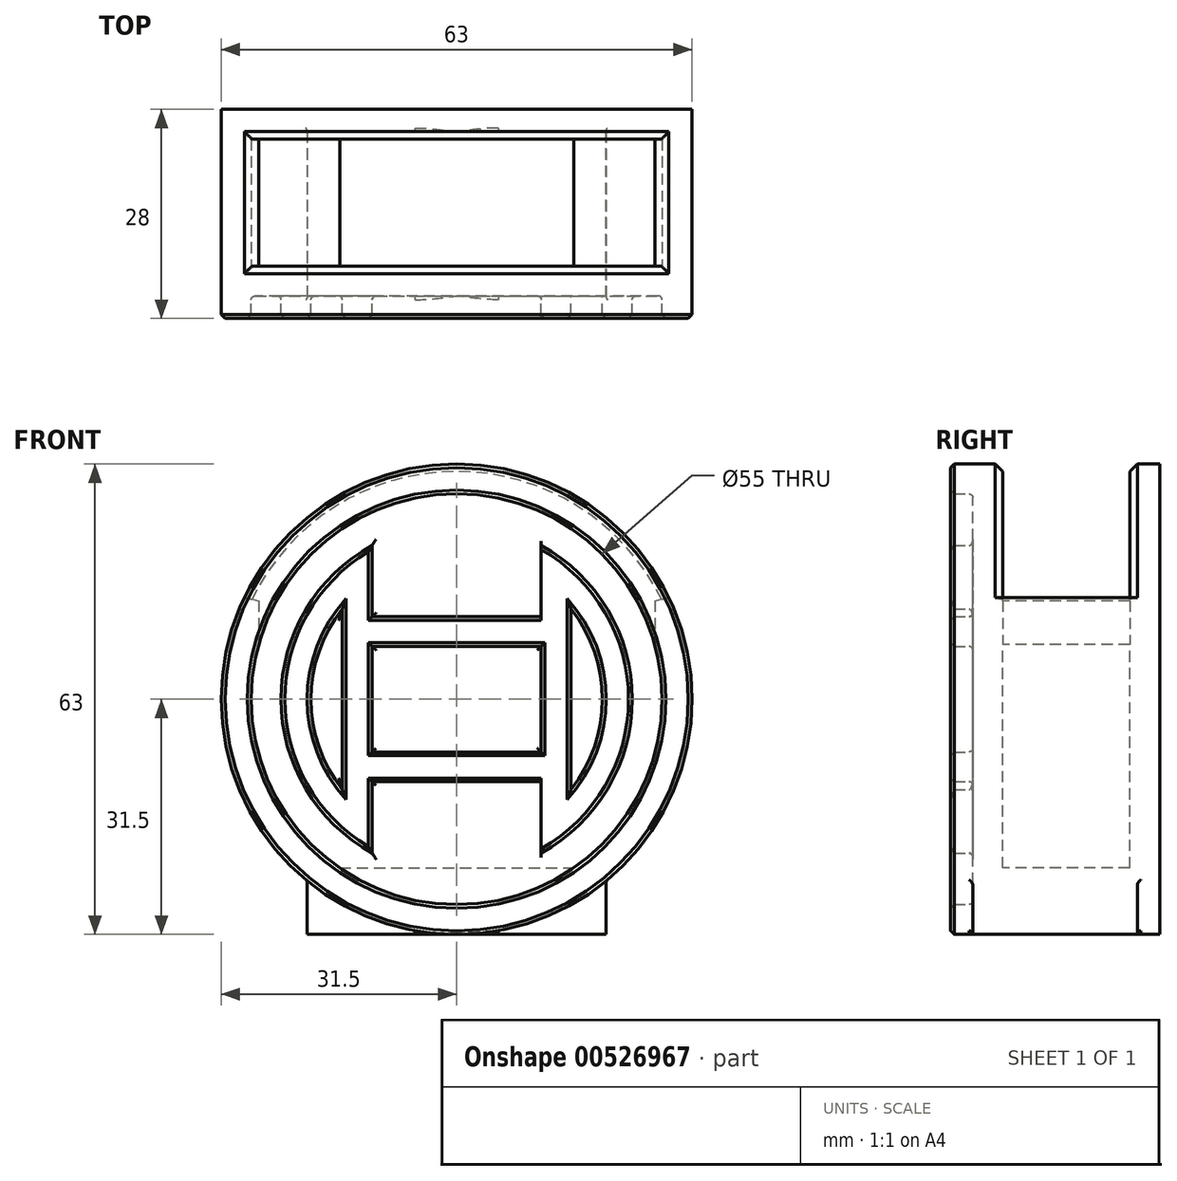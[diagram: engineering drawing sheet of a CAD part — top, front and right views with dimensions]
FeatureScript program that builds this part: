
annotation { "Feature Type Name" : "Feature", "Feature Type Description" : "" }
export const myFeature = defineFeature(function(context is Context, id is Id, definition is map)
    precondition{}
    {
        {
            var Q0;
            Q0=qCreatedBy(makeId("Front.planeOp"),FACE);
            var sketch = newSketch(context, id + "F0", { "sketchPlane" : qUnion([Q0])});
            skCircle(sketch, "E0", {"center": v(0, 0) * mm, "radius": 31.5 * mm});
            skCircle(sketch, "E1", {"center": v(0, 0) * mm, "radius": 27.5 * mm});
            skLineSegment(sketch, "E2", {"start": v(-15.3, 12.1) * mm, "end": v(-15.3, -12.1) * mm});
            skLineSegment(sketch, "E3", {"start": v(15.3, 12.1) * mm, "end": v(15.3, -12.1) * mm});
            skArc(sketch, "E4", {"start": v(-15.3, 12.1) * mm, "mid": v(-19.5, 0) * mm, "end": v(-15.3, -12.1) * mm});
            skArc(sketch, "E5", {"start": v(15.3, 12.1) * mm, "mid": v(19.5, 0) * mm, "end": v(15.3, -12.1) * mm});
            skLineSegment(sketch, "E6", {"start": v(-11.3, 20.6) * mm, "end": v(-11.3, -20.6) * mm});
            skLineSegment(sketch, "E7", {"start": v(11.3, 20.6) * mm, "end": v(11.3, -20.6) * mm});
            skArc(sketch, "E8", {"start": v(-11.3, 20.6) * mm, "mid": v(-23.5, 0) * mm, "end": v(-11.3, -20.6) * mm});
            skArc(sketch, "E9", {"start": v(11.3, 20.6) * mm, "mid": v(23.5, 0) * mm, "end": v(11.3, -20.6) * mm});
            skLineSegment(sketch, "E10", {"start": v(-11.3, 11.06) * mm, "end": v(11.3, 11.06) * mm});
            skLineSegment(sketch, "E11", {"start": v(-11.3, -11.06) * mm, "end": v(11.3, -11.06) * mm});
            skLineSegment(sketch, "E12", {"start": v(-11.3, 7.06) * mm, "end": v(11.3, 7.06) * mm});
            skLineSegment(sketch, "E13", {"start": v(-11.3, -7.06) * mm, "end": v(11.3, -7.06) * mm});
            skLineSegment(sketch, "E14", {"start": v(0, -11.06) * mm, "end": v(0, -27.5) * mm, "construction": true});
            skLineSegment(sketch, "E15", {"start": v(0, 11.06) * mm, "end": v(0, 27.5) * mm, "construction": true});
            skSolve(sketch);
        }
        {
            var Q0;
            Q0=makeQuery(id+"F0.imprint","IMPRINT",FACE,{"disambiguationData":[TD([[makeQuery(id+"F0.imprint","IMPRINT",EDGE,{"derivedFrom":sQuery(id+"F0.wireOp",EDGE,"E2")}),1.0]])]});
            var Q1;
            Q1=makeQuery(id+"F0.imprint","IMPRINT",FACE,{"disambiguationData":[TD([[makeQuery(id+"F0.imprint","IMPRINT",EDGE,{"derivedFrom":sQuery(id+"F0.wireOp",EDGE,"E3")}),-1.0]])]});
            var Q2;
            {var subQ0=sQuery(id+"F0.wireOp",EDGE,"E10");Q2=makeQuery(id+"F0.imprint","IMPRINT",FACE,{"disambiguationData":[TD([[makeQuery(id+"F0.imprint","IMPRINT",EDGE,{"derivedFrom":subQ0}),-1.0]])]});}
            var Q3;
            {var subQ0=sQuery(id+"F0.wireOp",EDGE,"E11");Q3=makeQuery(id+"F0.imprint","IMPRINT",FACE,{"disambiguationData":[TD([[makeQuery(id+"F0.imprint","IMPRINT",EDGE,{"derivedFrom":subQ0}),1.0]])]});}
            var Q4;
            Q4=makeQuery(id+"F0.imprint","IMPRINT",FACE,{"disambiguationData":[TD([[makeQuery(id+"F0.imprint","IMPRINT",EDGE,{"derivedFrom":sQuery(id+"F0.wireOp",EDGE,"E0")}),1.0]])]});
            var Q5;
            Q5=makeQuery(id+"F0.imprint","IMPRINT",FACE,{"disambiguationData":[TD([[makeQuery(id+"F0.imprint","IMPRINT",EDGE,{"derivedFrom":sQuery(id+"F0.wireOp",EDGE,"E1")}),1.0]])]});
            var Q6;
            Q6=makeQuery(id+"F0.imprint","IMPRINT",FACE,{"disambiguationData":[TD([[makeQuery(id+"F0.imprint","IMPRINT",EDGE,{"derivedFrom":sQuery(id+"F0.wireOp",EDGE,"E2")}),-1.0]])]});
            var Q7;
            {var subQ0=sQuery(id+"F0.wireOp",EDGE,"E12");Q7=makeQuery(id+"F0.imprint","IMPRINT",FACE,{"disambiguationData":[TD([[makeQuery(id+"F0.imprint","IMPRINT",EDGE,{"derivedFrom":subQ0}),-1.0]])]});}
            var Q8;
            Q8=makeQuery(id+"F0.imprint","IMPRINT",FACE,{"disambiguationData":[TD([[makeQuery(id+"F0.imprint","IMPRINT",EDGE,{"derivedFrom":sQuery(id+"F0.wireOp",EDGE,"E3")}),1.0]])]});
            extrude(context, id + "F1", {"entities" : qUnion([Q0, Q1, Q2, Q3, Q4, Q5, Q6, Q7, Q8]), "oppositeDirection" : true, "depth" : 25 * mm, "offsetDistance" : 25 * mm});
        }
        {
            var Q0;
            Q0=makeQuery(id+"F1.opExtrude","CAP_FACE",FACE,{"disambiguationData":[OSD([sQuery(id+"F0.wireOp",EDGE,"E0")])],"isStart":true});
            var Q1;
            Q1=makeQuery(id+"F1.opExtrude","SWEPT_BODY",BODY,{"disambiguationData":[OSD([sQuery(id+"F0.wireOp",EDGE,"E0")])]});
            shell(context, id + "F2", {"isHollow" : true, "entities" : qUnion([Q0]), "parts" : qUnion([Q1]), "thickness" : 4 * mm});
        }
        {
            var Q0;
            Q0=makeQuery(id+"F0.imprint","IMPRINT",FACE,{"disambiguationData":[TD([[makeQuery(id+"F0.imprint","IMPRINT",EDGE,{"derivedFrom":sQuery(id+"F0.wireOp",EDGE,"E0")}),1.0]])]});
            var Q1;
            Q1=makeQuery(id+"F0.imprint","IMPRINT",FACE,{"disambiguationData":[TD([[makeQuery(id+"F0.imprint","IMPRINT",EDGE,{"derivedFrom":sQuery(id+"F0.wireOp",EDGE,"E2")}),1.0]])]});
            var Q2;
            {var subQ0=sQuery(id+"F0.wireOp",EDGE,"E10");Q2=makeQuery(id+"F0.imprint","IMPRINT",FACE,{"disambiguationData":[TD([[makeQuery(id+"F0.imprint","IMPRINT",EDGE,{"derivedFrom":subQ0}),-1.0]])]});}
            var Q3;
            {var subQ0=sQuery(id+"F0.wireOp",EDGE,"E11");Q3=makeQuery(id+"F0.imprint","IMPRINT",FACE,{"disambiguationData":[TD([[makeQuery(id+"F0.imprint","IMPRINT",EDGE,{"derivedFrom":subQ0}),1.0]])]});}
            var Q4;
            Q4=makeQuery(id+"F0.imprint","IMPRINT",FACE,{"disambiguationData":[TD([[makeQuery(id+"F0.imprint","IMPRINT",EDGE,{"derivedFrom":sQuery(id+"F0.wireOp",EDGE,"E3")}),-1.0]])]});
            extrude(context, id + "F3", {"entities" : qUnion([Q0, Q1, Q2, Q3, Q4]), "operationType" : NewBodyOperationType.ADD, "depth" : 3 * mm, "offsetDistance" : 25 * mm});
        }
        {
            var Q0;
            Q0=makeQuery(id+"F3.opExtrude","CAP_EDGE",EDGE,{"disambiguationData":[OSD([sQuery(id+"F0.wireOp",EDGE,"E1")])],"isStart":true});
            var Q1;
            {var subQ0=sQuery(id+"F0.wireOp",EDGE,"E6");Q1=makeQuery(id+"F3.opExtrude","CAP_EDGE",EDGE,{"disambiguationData":[OSD([subQ0]),TDD([makeQuery(id+"F0.imprint","IMPRINT",EDGE,{"disambiguationData":[TD([[makeQuery(id+"F0.imprint","INTERSECT",VERTEX,{"disambiguationData":[OD(0.0)],"derivedFrom":[subQ0,sQuery(id+"F0.wireOp",EDGE,"E8")]}),-1.0]])],"derivedFrom":subQ0})])],"isStart":true});}
            var Q2;
            Q2=makeQuery(id+"F3.opExtrude","CAP_EDGE",EDGE,{"disambiguationData":[OSD([sQuery(id+"F0.wireOp",EDGE,"E10")])],"isStart":true});
            var Q3;
            {var subQ0=sQuery(id+"F0.wireOp",EDGE,"E7");Q3=makeQuery(id+"F3.opExtrude","CAP_EDGE",EDGE,{"disambiguationData":[OSD([subQ0]),TDD([makeQuery(id+"F0.imprint","IMPRINT",EDGE,{"disambiguationData":[TD([[makeQuery(id+"F0.imprint","INTERSECT",VERTEX,{"disambiguationData":[OD(0.0)],"derivedFrom":[subQ0,sQuery(id+"F0.wireOp",EDGE,"E9")]}),-1.0]])],"derivedFrom":subQ0})])],"isStart":true});}
            var Q4;
            Q4=makeQuery(id+"F3.opExtrude","CAP_EDGE",EDGE,{"disambiguationData":[OSD([sQuery(id+"F0.wireOp",EDGE,"E8")])],"isStart":true});
            var Q5;
            Q5=makeQuery(id+"F3.opExtrude","CAP_EDGE",EDGE,{"disambiguationData":[OSD([sQuery(id+"F0.wireOp",EDGE,"E9")])],"isStart":true});
            var Q6;
            {var subQ0=sQuery(id+"F0.wireOp",EDGE,"E6");Q6=makeQuery(id+"F3.opExtrude","CAP_EDGE",EDGE,{"disambiguationData":[OSD([subQ0]),TDD([makeQuery(id+"F0.imprint","IMPRINT",EDGE,{"disambiguationData":[TD([[makeQuery(id+"F0.imprint","INTERSECT",VERTEX,{"disambiguationData":[OD(1.0)],"derivedFrom":[subQ0,sQuery(id+"F0.wireOp",EDGE,"E8")]}),1.0]])],"derivedFrom":subQ0})])],"isStart":true});}
            var Q7;
            Q7=makeQuery(id+"F3.opExtrude","CAP_EDGE",EDGE,{"disambiguationData":[OSD([sQuery(id+"F0.wireOp",EDGE,"E11")])],"isStart":true});
            var Q8;
            {var subQ0=sQuery(id+"F0.wireOp",EDGE,"E7");Q8=makeQuery(id+"F3.opExtrude","CAP_EDGE",EDGE,{"disambiguationData":[OSD([subQ0]),TDD([makeQuery(id+"F0.imprint","IMPRINT",EDGE,{"disambiguationData":[TD([[makeQuery(id+"F0.imprint","INTERSECT",VERTEX,{"disambiguationData":[OD(1.0)],"derivedFrom":[subQ0,sQuery(id+"F0.wireOp",EDGE,"E9")]}),1.0]])],"derivedFrom":subQ0})])],"isStart":true});}
            var Q9;
            Q9=makeQuery(id+"F3.opExtrude","CAP_EDGE",EDGE,{"disambiguationData":[OSD([sQuery(id+"F0.wireOp",EDGE,"E12")])],"isStart":true});
            var Q10;
            {var subQ0=sQuery(id+"F0.wireOp",EDGE,"E6");Q10=makeQuery(id+"F3.opExtrude","CAP_EDGE",EDGE,{"disambiguationData":[OSD([subQ0]),TDD([makeQuery(id+"F0.imprint","IMPRINT",EDGE,{"disambiguationData":[TD([[makeQuery(id+"F0.imprint","INTERSECT",VERTEX,{"derivedFrom":[subQ0,sQuery(id+"F0.wireOp",EDGE,"E12")]}),-1.0]])],"derivedFrom":subQ0})])],"isStart":true});}
            var Q11;
            Q11=makeQuery(id+"F3.opExtrude","CAP_EDGE",EDGE,{"disambiguationData":[OSD([sQuery(id+"F0.wireOp",EDGE,"E13")])],"isStart":true});
            var Q12;
            {var subQ0=sQuery(id+"F0.wireOp",EDGE,"E7");Q12=makeQuery(id+"F3.opExtrude","CAP_EDGE",EDGE,{"disambiguationData":[OSD([subQ0]),TDD([makeQuery(id+"F0.imprint","IMPRINT",EDGE,{"disambiguationData":[TD([[makeQuery(id+"F0.imprint","INTERSECT",VERTEX,{"derivedFrom":[subQ0,sQuery(id+"F0.wireOp",EDGE,"E12")]}),-1.0]])],"derivedFrom":subQ0})])],"isStart":true});}
            var Q13;
            Q13=makeQuery(id+"F3.opExtrude","CAP_EDGE",EDGE,{"disambiguationData":[OSD([sQuery(id+"F0.wireOp",EDGE,"E5")])],"isStart":true});
            var Q14;
            Q14=makeQuery(id+"F3.opExtrude","CAP_EDGE",EDGE,{"disambiguationData":[OSD([sQuery(id+"F0.wireOp",EDGE,"E3")])],"isStart":true});
            var Q15;
            Q15=makeQuery(id+"F3.opExtrude","CAP_EDGE",EDGE,{"disambiguationData":[OSD([sQuery(id+"F0.wireOp",EDGE,"E4")])],"isStart":true});
            var Q16;
            Q16=makeQuery(id+"F3.opExtrude","CAP_EDGE",EDGE,{"disambiguationData":[OSD([sQuery(id+"F0.wireOp",EDGE,"E2")])],"isStart":true});
            fillet(context, id + "F4", {"entities" : qUnion([Q0, Q1, Q2, Q3, Q4, Q5, Q6, Q7, Q8, Q9, Q10, Q11, Q12, Q13, Q14, Q15, Q16]), "radius" : .5 * mm, "tangentPropagation" : true, "allowEdgeOverflow" : false});
        }
        {
            var Q0;
            Q0=makeQuery(id+"F3.opExtrude","CAP_EDGE",EDGE,{"disambiguationData":[OSD([sQuery(id+"F0.wireOp",EDGE,"E0")])],"isStart":false});
            var Q1;
            Q1=makeQuery(id+"F3.opExtrude","CAP_EDGE",EDGE,{"disambiguationData":[OSD([sQuery(id+"F0.wireOp",EDGE,"E8")])],"isStart":false});
            var Q2;
            {var subQ0=sQuery(id+"F0.wireOp",EDGE,"E6");Q2=makeQuery(id+"F3.opExtrude","CAP_EDGE",EDGE,{"disambiguationData":[OSD([subQ0]),TDD([makeQuery(id+"F0.imprint","IMPRINT",EDGE,{"disambiguationData":[TD([[makeQuery(id+"F0.imprint","INTERSECT",VERTEX,{"disambiguationData":[OD(1.0)],"derivedFrom":[subQ0,sQuery(id+"F0.wireOp",EDGE,"E8")]}),1.0]])],"derivedFrom":subQ0})])],"isStart":false});}
            var Q3;
            Q3=makeQuery(id+"F3.opExtrude","CAP_EDGE",EDGE,{"disambiguationData":[OSD([sQuery(id+"F0.wireOp",EDGE,"E11")])],"isStart":false});
            var Q4;
            {var subQ0=sQuery(id+"F0.wireOp",EDGE,"E7");Q4=makeQuery(id+"F3.opExtrude","CAP_EDGE",EDGE,{"disambiguationData":[OSD([subQ0]),TDD([makeQuery(id+"F0.imprint","IMPRINT",EDGE,{"disambiguationData":[TD([[makeQuery(id+"F0.imprint","INTERSECT",VERTEX,{"disambiguationData":[OD(1.0)],"derivedFrom":[subQ0,sQuery(id+"F0.wireOp",EDGE,"E9")]}),1.0]])],"derivedFrom":subQ0})])],"isStart":false});}
            var Q5;
            Q5=makeQuery(id+"F3.opExtrude","CAP_EDGE",EDGE,{"disambiguationData":[OSD([sQuery(id+"F0.wireOp",EDGE,"E9")])],"isStart":false});
            var Q6;
            Q6=makeQuery(id+"F3.opExtrude","CAP_EDGE",EDGE,{"disambiguationData":[OSD([sQuery(id+"F0.wireOp",EDGE,"E13")])],"isStart":false});
            var Q7;
            {var subQ0=sQuery(id+"F0.wireOp",EDGE,"E6");Q7=makeQuery(id+"F3.opExtrude","CAP_EDGE",EDGE,{"disambiguationData":[OSD([subQ0]),TDD([makeQuery(id+"F0.imprint","IMPRINT",EDGE,{"disambiguationData":[TD([[makeQuery(id+"F0.imprint","INTERSECT",VERTEX,{"derivedFrom":[subQ0,sQuery(id+"F0.wireOp",EDGE,"E12")]}),-1.0]])],"derivedFrom":subQ0})])],"isStart":false});}
            var Q8;
            {var subQ0=sQuery(id+"F0.wireOp",EDGE,"E7");Q8=makeQuery(id+"F3.opExtrude","CAP_EDGE",EDGE,{"disambiguationData":[OSD([subQ0]),TDD([makeQuery(id+"F0.imprint","IMPRINT",EDGE,{"disambiguationData":[TD([[makeQuery(id+"F0.imprint","INTERSECT",VERTEX,{"derivedFrom":[subQ0,sQuery(id+"F0.wireOp",EDGE,"E12")]}),-1.0]])],"derivedFrom":subQ0})])],"isStart":false});}
            var Q9;
            Q9=makeQuery(id+"F3.opExtrude","CAP_EDGE",EDGE,{"disambiguationData":[OSD([sQuery(id+"F0.wireOp",EDGE,"E4")])],"isStart":false});
            var Q10;
            Q10=makeQuery(id+"F3.opExtrude","CAP_EDGE",EDGE,{"disambiguationData":[OSD([sQuery(id+"F0.wireOp",EDGE,"E2")])],"isStart":false});
            var Q11;
            Q11=makeQuery(id+"F3.opExtrude","CAP_EDGE",EDGE,{"disambiguationData":[OSD([sQuery(id+"F0.wireOp",EDGE,"E12")])],"isStart":false});
            var Q12;
            Q12=makeQuery(id+"F3.opExtrude","CAP_EDGE",EDGE,{"disambiguationData":[OSD([sQuery(id+"F0.wireOp",EDGE,"E10")])],"isStart":false});
            var Q13;
            {var subQ0=sQuery(id+"F0.wireOp",EDGE,"E6");Q13=makeQuery(id+"F3.opExtrude","CAP_EDGE",EDGE,{"disambiguationData":[OSD([subQ0]),TDD([makeQuery(id+"F0.imprint","IMPRINT",EDGE,{"disambiguationData":[TD([[makeQuery(id+"F0.imprint","INTERSECT",VERTEX,{"disambiguationData":[OD(0.0)],"derivedFrom":[subQ0,sQuery(id+"F0.wireOp",EDGE,"E8")]}),-1.0]])],"derivedFrom":subQ0})])],"isStart":false});}
            var Q14;
            {var subQ0=sQuery(id+"F0.wireOp",EDGE,"E7");Q14=makeQuery(id+"F3.opExtrude","CAP_EDGE",EDGE,{"disambiguationData":[OSD([subQ0]),TDD([makeQuery(id+"F0.imprint","IMPRINT",EDGE,{"disambiguationData":[TD([[makeQuery(id+"F0.imprint","INTERSECT",VERTEX,{"disambiguationData":[OD(0.0)],"derivedFrom":[subQ0,sQuery(id+"F0.wireOp",EDGE,"E9")]}),-1.0]])],"derivedFrom":subQ0})])],"isStart":false});}
            var Q15;
            Q15=makeQuery(id+"F3.opExtrude","CAP_EDGE",EDGE,{"disambiguationData":[OSD([sQuery(id+"F0.wireOp",EDGE,"E3")])],"isStart":false});
            var Q16;
            Q16=makeQuery(id+"F3.opExtrude","CAP_EDGE",EDGE,{"disambiguationData":[OSD([sQuery(id+"F0.wireOp",EDGE,"E5")])],"isStart":false});
            var Q17;
            Q17=makeQuery(id+"F3.opExtrude","CAP_EDGE",EDGE,{"disambiguationData":[OSD([sQuery(id+"F0.wireOp",EDGE,"E1")])],"isStart":false});
            chamfer(context, id + "F5", {"entities" : qUnion([Q0, Q1, Q2, Q3, Q4, Q5, Q6, Q7, Q8, Q9, Q10, Q11, Q12, Q13, Q14, Q15, Q16, Q17]), "width" : .5 * mm, "tangentPropagation" : true});
        }
        {
            var Q0;
            Q0=qCreatedBy(makeId("Top.planeOp"),FACE);
            var sketch = newSketch(context, id + "F6", { "sketchPlane" : qUnion([Q0])});
            skLineSegment(sketch, "E16.bottom", {"start": v(-26.5, 21) * mm, "end": v(26.5, 21) * mm});
            skLineSegment(sketch, "E16.top", {"start": v(-26.5, 4) * mm, "end": v(26.5, 4) * mm});
            skLineSegment(sketch, "E16.left", {"start": v(-26.5, 21) * mm, "end": v(-26.5, 4) * mm});
            skLineSegment(sketch, "E16.right", {"start": v(26.5, 21) * mm, "end": v(26.5, 4) * mm});
            skLineSegment(sketch, "E17.0", {"start": v(31.5, 25) * mm, "end": v(-31.5, 25) * mm, "construction": true});
            skLineSegment(sketch, "E18", {"start": v(-31.5, 25) * mm, "end": v(-31.5, 0) * mm, "construction": true});
            skLineSegment(sketch, "E19", {"start": v(31.5, 25) * mm, "end": v(31.5, 0) * mm, "construction": true});
            skLineSegment(sketch, "E20", {"start": v(-31.5, 0) * mm, "end": v(31.5, 0) * mm, "construction": true});
            skSolve(sketch);
        }
        {
            var Q0;
            Q0 = qSketchRegion(id + "F6", true);
            extrude(context, id + "F7", {"entities" : qUnion([Q0]), "operationType" : NewBodyOperationType.REMOVE, "endBound" : BoundingType.THROUGH_ALL, "depth" : 25 * mm, "offsetDistance" : 25 * mm});
        }
        {
            var Q0;
            {var subQ0=sQuery(id+"F0.wireOp",EDGE,"E0");Q0=makeQuery(id+"F7.boolean.opBoolean","INTERSECT",EDGE,{"derivedFrom":[makeQuery(id+"F3.boolean.opBoolean","MERGE",FACE,{"derivedFrom":[makeQuery(id+"F1.opExtrude","SWEPT_FACE",FACE,{"disambiguationData":[OSD([subQ0])]}),makeQuery(id+"F3.opExtrude","SWEPT_FACE",FACE,{"disambiguationData":[OSD([subQ0])]})]}),makeQuery(id+"F7.opExtrude","SWEPT_FACE",FACE,{"disambiguationData":[OSD([sQuery(id+"F6.wireOp",EDGE,"E16.top")])]})]});}
            var Q1;
            {var subQ0=sQuery(id+"F0.wireOp",EDGE,"E0");Q1=makeQuery(id+"F7.boolean.opBoolean","INTERSECT",EDGE,{"derivedFrom":[makeQuery(id+"F3.boolean.opBoolean","MERGE",FACE,{"derivedFrom":[makeQuery(id+"F1.opExtrude","SWEPT_FACE",FACE,{"disambiguationData":[OSD([subQ0])]}),makeQuery(id+"F3.opExtrude","SWEPT_FACE",FACE,{"disambiguationData":[OSD([subQ0])]})]}),makeQuery(id+"F7.opExtrude","SWEPT_FACE",FACE,{"disambiguationData":[OSD([sQuery(id+"F6.wireOp",EDGE,"E16.left")])]})]});}
            var Q2;
            {var subQ0=sQuery(id+"F0.wireOp",EDGE,"E0");Q2=makeQuery(id+"F7.boolean.opBoolean","INTERSECT",EDGE,{"derivedFrom":[makeQuery(id+"F3.boolean.opBoolean","MERGE",FACE,{"derivedFrom":[makeQuery(id+"F1.opExtrude","SWEPT_FACE",FACE,{"disambiguationData":[OSD([subQ0])]}),makeQuery(id+"F3.opExtrude","SWEPT_FACE",FACE,{"disambiguationData":[OSD([subQ0])]})]}),makeQuery(id+"F7.opExtrude","SWEPT_FACE",FACE,{"disambiguationData":[OSD([sQuery(id+"F6.wireOp",EDGE,"E16.bottom")])]})]});}
            var Q3;
            {var subQ0=sQuery(id+"F0.wireOp",EDGE,"E0");Q3=makeQuery(id+"F7.boolean.opBoolean","INTERSECT",EDGE,{"derivedFrom":[makeQuery(id+"F3.boolean.opBoolean","MERGE",FACE,{"derivedFrom":[makeQuery(id+"F1.opExtrude","SWEPT_FACE",FACE,{"disambiguationData":[OSD([subQ0])]}),makeQuery(id+"F3.opExtrude","SWEPT_FACE",FACE,{"disambiguationData":[OSD([subQ0])]})]}),makeQuery(id+"F7.opExtrude","SWEPT_FACE",FACE,{"disambiguationData":[OSD([sQuery(id+"F6.wireOp",EDGE,"E16.right")])]})]});}
            chamfer(context, id + "F8", {"entities" : qUnion([Q0, Q1, Q2, Q3]), "width" : 1 * mm, "tangentPropagation" : true});
        }
        {
            var Q0;
            Q0=qCreatedBy(makeId("Front.planeOp"),FACE);
            var sketch = newSketch(context, id + "F9", { "sketchPlane" : qUnion([Q0])});
            skLineSegment(sketch, "E21", {"start": v(0, 0) * mm, "end": v(0, -56.06) * mm, "construction": true});
            skLineSegment(sketch, "E22", {"start": v(-20, -31.5) * mm, "end": v(20, -31.5) * mm});
            skLineSegment(sketch, "E23", {"start": v(-20, -31.5) * mm, "end": v(-20, -22.61) * mm});
            skLineSegment(sketch, "E24", {"start": v(-20, -22.61) * mm, "end": v(20, -22.61) * mm});
            skLineSegment(sketch, "E25", {"start": v(20, -31.5) * mm, "end": v(20, -22.61) * mm});
            skSolve(sketch);
        }
        {
            var Q0;
            Q0 = qSketchRegion(id + "F9", true);
            extrude(context, id + "F10", {"entities" : qUnion([Q0]), "operationType" : NewBodyOperationType.ADD, "oppositeDirection" : true, "depth" : 22 * mm, "offsetDistance" : 25 * mm});
        }
        {
            var Q0;
            {var subQ0=sQuery(id+"F0.wireOp",EDGE,"E0");Q0=makeQuery(id+"F10.boolean.opBoolean","INTERSECT",EDGE,{"derivedFrom":[makeQuery(id+"F3.boolean.opBoolean","MERGE",FACE,{"derivedFrom":[makeQuery(id+"F1.opExtrude","SWEPT_FACE",FACE,{"disambiguationData":[OSD([subQ0])]}),makeQuery(id+"F3.opExtrude","SWEPT_FACE",FACE,{"disambiguationData":[OSD([subQ0])]})]}),makeQuery(id+"F10.opExtrude","SWEPT_FACE",FACE,{"disambiguationData":[OSD([sQuery(id+"F9.wireOp",EDGE,"E23")])]})]});}
            var Q1;
            {var subQ0=sQuery(id+"F0.wireOp",EDGE,"E0");Q1=makeQuery(id+"F10.boolean.opBoolean","INTERSECT",EDGE,{"disambiguationData":[OD(0.0)],"derivedFrom":[makeQuery(id+"F3.boolean.opBoolean","MERGE",FACE,{"derivedFrom":[makeQuery(id+"F1.opExtrude","SWEPT_FACE",FACE,{"disambiguationData":[OSD([subQ0])]}),makeQuery(id+"F3.opExtrude","SWEPT_FACE",FACE,{"disambiguationData":[OSD([subQ0])]})]}),makeQuery(id+"F10.opExtrude","CAP_FACE",FACE,{"disambiguationData":[OSD([sQuery(id+"F9.wireOp",EDGE,"E22"),sQuery(id+"F9.wireOp",EDGE,"E23"),sQuery(id+"F9.wireOp",EDGE,"E24"),sQuery(id+"F9.wireOp",EDGE,"E25")])],"isStart":true})]});}
            var Q2;
            {var subQ0=sQuery(id+"F0.wireOp",EDGE,"E0");Q2=makeQuery(id+"F10.boolean.opBoolean","INTERSECT",EDGE,{"disambiguationData":[OD(0.0)],"derivedFrom":[makeQuery(id+"F3.boolean.opBoolean","MERGE",FACE,{"derivedFrom":[makeQuery(id+"F1.opExtrude","SWEPT_FACE",FACE,{"disambiguationData":[OSD([subQ0])]}),makeQuery(id+"F3.opExtrude","SWEPT_FACE",FACE,{"disambiguationData":[OSD([subQ0])]})]}),makeQuery(id+"F10.opExtrude","CAP_FACE",FACE,{"disambiguationData":[OSD([sQuery(id+"F9.wireOp",EDGE,"E22"),sQuery(id+"F9.wireOp",EDGE,"E23"),sQuery(id+"F9.wireOp",EDGE,"E24"),sQuery(id+"F9.wireOp",EDGE,"E25")])],"isStart":false})]});}
            var Q3;
            {var subQ0=sQuery(id+"F0.wireOp",EDGE,"E0");Q3=makeQuery(id+"F10.boolean.opBoolean","INTERSECT",EDGE,{"derivedFrom":[makeQuery(id+"F3.boolean.opBoolean","MERGE",FACE,{"derivedFrom":[makeQuery(id+"F1.opExtrude","SWEPT_FACE",FACE,{"disambiguationData":[OSD([subQ0])]}),makeQuery(id+"F3.opExtrude","SWEPT_FACE",FACE,{"disambiguationData":[OSD([subQ0])]})]}),makeQuery(id+"F10.opExtrude","SWEPT_FACE",FACE,{"disambiguationData":[OSD([sQuery(id+"F9.wireOp",EDGE,"E25")])]})]});}
            fillet(context, id + "F11", {"entities" : qUnion([Q0, Q1, Q2, Q3]), "radius" : .5 * mm, "tangentPropagation" : true, "allowEdgeOverflow" : false});
        }
    });
